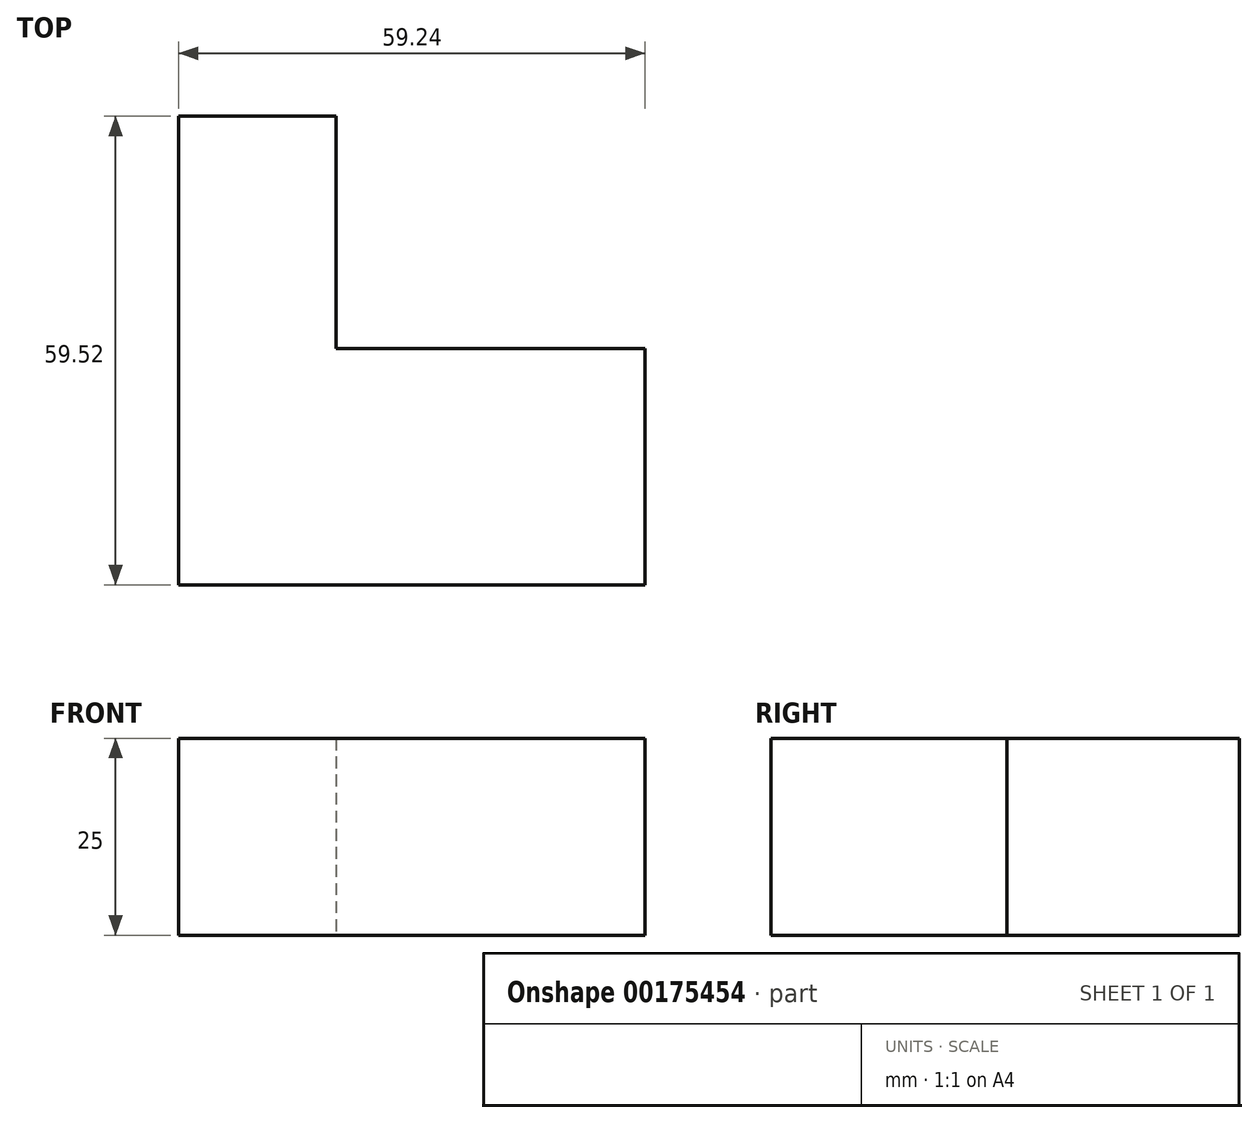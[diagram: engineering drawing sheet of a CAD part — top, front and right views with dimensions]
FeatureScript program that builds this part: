
annotation { "Feature Type Name" : "Feature", "Feature Type Description" : "" }
export const myFeature = defineFeature(function(context is Context, id is Id, definition is map)
    precondition{}
    {
        {
            var Q0;
            Q0=qCreatedBy(makeId("Top.planeOp"),FACE);
            var sketch = newSketch(context, id + "F0", { "sketchPlane" : qUnion([Q0])});
            skLineSegment(sketch, "E0", {"start": v(-54.98, 54.87) * mm, "end": v(-34.98, 54.87) * mm});
            skLineSegment(sketch, "E1", {"start": v(-54.98, 54.87) * mm, "end": v(-54.98, -5.13) * mm});
            skLineSegment(sketch, "E2", {"start": v(-55.74, -4.65) * mm, "end": v(4.26, -4.65) * mm});
            skLineSegment(sketch, "E3", {"start": v(4.26, -4.65) * mm, "end": v(4.26, 25.35) * mm});
            skLineSegment(sketch, "E4", {"start": v(4.26, 25.35) * mm, "end": v(-34.98, 25.35) * mm});
            skLineSegment(sketch, "E5", {"start": v(-34.98, 25.35) * mm, "end": v(-34.98, 54.87) * mm});
            skSolve(sketch);
        }
        {
            var Q0;
            {var subQ4=sQuery(id+"F0.wireOp",EDGE,"E0");Q0=makeQuery(id+"F0.imprint","IMPRINT",FACE,{"disambiguationData":[TD([[makeQuery(id+"F0.imprint","IMPRINT",EDGE,{"derivedFrom":subQ4}),-1.0]])]});}
            extrude(context, id + "F1", {"entities" : qUnion([Q0]), "depth" : 25 * mm});
        }
    });
